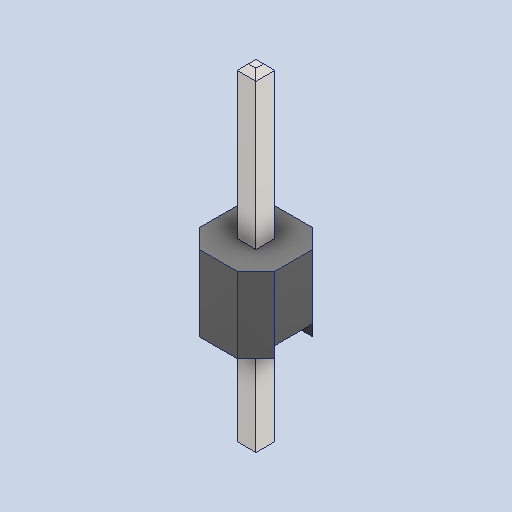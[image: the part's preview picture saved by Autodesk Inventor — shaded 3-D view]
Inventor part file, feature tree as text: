
AUTODESK INVENTOR PART (.ipt)
format: ipt  version: 2024 (Build 280153000, 153)  size: 103,424 bytes
history: native  units: in
note: dims shown in document units (in); Inventor stores cm internally (conversion verified against a paired STEP export)
features: chamfer x1
ambient origin geometry x8: Origin, YZ Plane, XZ Plane, XY Plane, X Axis, Y Axis, Z Axis, Center Point
bodies: Solid1 (feature_tree)
feature tree (1):
  chamfer  "Chamfer2"  [1 undecoded]
note: 1 required parameter value undecoded (feature->parameter linkage not recoverable at this tier; creation-order binding heuristic only, values carry confidence <= 0.55)
